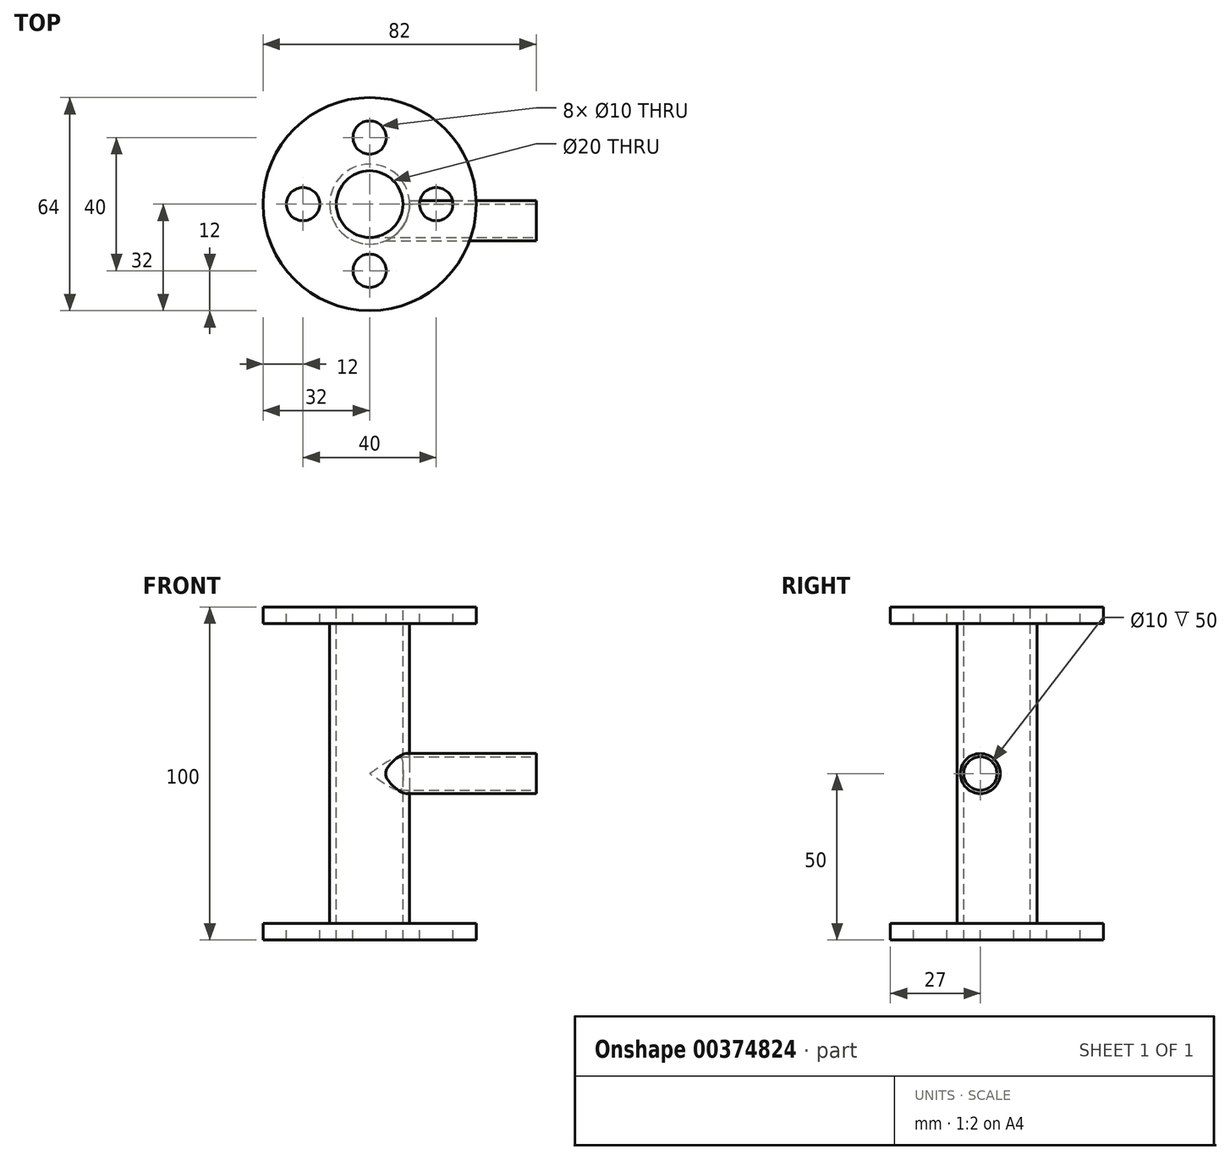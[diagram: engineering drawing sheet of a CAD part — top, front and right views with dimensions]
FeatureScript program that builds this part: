
annotation { "Feature Type Name" : "Feature", "Feature Type Description" : "" }
export const myFeature = defineFeature(function(context is Context, id is Id, definition is map)
    precondition{}
    {
        {
            var Q0;
            Q0=qCreatedBy(makeId("Top.planeOp"),FACE);
            var sketch = newSketch(context, id + "F0", { "sketchPlane" : qUnion([Q0])});
            skCircle(sketch, "E0", {"center": v(0, 0) * mm, "radius": 12 * mm});
            skSolve(sketch);
        }
        {
            var Q0;
            Q0 = qSketchRegion(id + "F0", true);
            extrude(context, id + "F1", {"entities" : qUnion([Q0]), "depth" : 100 * mm, "offsetDistance" : 25 * mm});
        }
        {
            var Q0;
            Q0=makeQuery(id+"F1.opExtrude","CAP_FACE",FACE,{"disambiguationData":[OSD([sQuery(id+"F0.wireOp",EDGE,"E0")])],"isStart":false});
            var sketch = newSketch(context, id + "F2", { "sketchPlane" : qUnion([Q0])});
            skCircle(sketch, "E1", {"center": v(0, 0) * mm, "radius": 10 * mm});
            skSolve(sketch);
        }
        {
            var Q0;
            Q0=makeQuery(id+"F2.imprint","IMPRINT",FACE,{"disambiguationData":[TD([[makeQuery(id+"F2.imprint","IMPRINT",EDGE,{"derivedFrom":sQuery(id+"F2.wireOp",EDGE,"E1")}),1.0]])]});
            var Q1;
            Q1=makeQuery(id+"F1.opExtrude","CAP_FACE",FACE,{"disambiguationData":[OSD([sQuery(id+"F0.wireOp",EDGE,"E0")])],"isStart":true});
            extrude(context, id + "F3", {"entities" : qUnion([Q0]), "operationType" : NewBodyOperationType.REMOVE, "endBound" : BoundingType.UP_TO_SURFACE, "oppositeDirection" : true, "depth" : 25 * mm, "endBoundEntityFace" : qUnion([Q1]), "offsetDistance" : 25 * mm});
        }
        {
            var Q0;
            Q0=makeQuery(id+"F1.opExtrude","CAP_FACE",FACE,{"disambiguationData":[OSD([sQuery(id+"F0.wireOp",EDGE,"E0")])],"isStart":true});
            var sketch = newSketch(context, id + "F4", { "sketchPlane" : qUnion([Q0])});
            skCircle(sketch, "E2", {"center": v(0, 0) * mm, "radius": 32 * mm});
            skSolve(sketch);
        }
        {
            var Q0;
            Q0=makeQuery(id+"F4.imprint","IMPRINT",FACE,{"disambiguationData":[TD([[makeQuery(id+"F4.imprint","IMPRINT",EDGE,{"derivedFrom":sQuery(id+"F4.wireOp",EDGE,"E2")}),1.0]])]});
            extrude(context, id + "F5", {"entities" : qUnion([Q0]), "operationType" : NewBodyOperationType.ADD, "oppositeDirection" : true, "depth" : 5 * mm, "offsetDistance" : 25 * mm});
        }
        {
            var Q0;
            Q0=makeQuery(id+"F1.opExtrude","CAP_FACE",FACE,{"disambiguationData":[OSD([sQuery(id+"F0.wireOp",EDGE,"E0")])],"isStart":false});
            var sketch = newSketch(context, id + "F6", { "sketchPlane" : qUnion([Q0])});
            skCircle(sketch, "E3", {"center": v(0, 0) * mm, "radius": 32 * mm});
            skSolve(sketch);
        }
        {
            var Q0;
            Q0=makeQuery(id+"F6.imprint","IMPRINT",FACE,{"disambiguationData":[TD([[makeQuery(id+"F6.imprint","IMPRINT",EDGE,{"derivedFrom":sQuery(id+"F6.wireOp",EDGE,"E3")}),1.0]])]});
            extrude(context, id + "F7", {"entities" : qUnion([Q0]), "operationType" : NewBodyOperationType.ADD, "oppositeDirection" : true, "depth" : 5 * mm, "offsetDistance" : 25 * mm});
        }
        {
            var Q0;
            {var subQ0=sQuery(id+"F0.wireOp",EDGE,"E0");Q0=makeQuery(id+"F7.boolean.opBoolean","MERGE",FACE,{"derivedFrom":[makeQuery(id+"F1.opExtrude","CAP_FACE",FACE,{"disambiguationData":[OSD([subQ0])],"isStart":false}),makeQuery(id+"F7.opExtrude","CAP_FACE",FACE,{"disambiguationData":[OSD([subQ0,sQuery(id+"F6.wireOp",EDGE,"E3")])],"isStart":true})]});}
            var sketch = newSketch(context, id + "F8", { "sketchPlane" : qUnion([Q0])});
            skCircle(sketch, "E4", {"center": v(0, 20) * mm, "radius": 5 * mm});
            skCircle(sketch, "E5.1.0", {"center": v(-20, 0) * mm, "radius": 5 * mm});
            skCircle(sketch, "E5.2.0", {"center": v(0, -20) * mm, "radius": 5 * mm});
            skCircle(sketch, "E5.3.0", {"center": v(20, 0) * mm, "radius": 5 * mm});
            skPoint(sketch, "E5.center", {"position": v(0, 0) * mm});
            skSolve(sketch);
        }
        {
            var Q0;
            Q0 = qSketchRegion(id + "F8", true);
            var Q1;
            {var subQ0=sQuery(id+"F0.wireOp",EDGE,"E0");Q1=makeQuery(id+"F5.boolean.opBoolean","MERGE",FACE,{"derivedFrom":[makeQuery(id+"F1.opExtrude","CAP_FACE",FACE,{"disambiguationData":[OSD([subQ0])],"isStart":true}),makeQuery(id+"F5.opExtrude","CAP_FACE",FACE,{"disambiguationData":[OSD([subQ0,sQuery(id+"F4.wireOp",EDGE,"E2")])],"isStart":true})]});}
            extrude(context, id + "F9", {"entities" : qUnion([Q0]), "operationType" : NewBodyOperationType.REMOVE, "endBound" : BoundingType.UP_TO_SURFACE, "oppositeDirection" : true, "depth" : 25 * mm, "endBoundEntityFace" : qUnion([Q1]), "offsetDistance" : 25 * mm});
        }
        {
            var Q0;
            Q0=qCreatedBy(makeId("Right.planeOp"),FACE);
            var sketch = newSketch(context, id + "F10", { "sketchPlane" : qUnion([Q0])});
            skLineSegment(sketch, "E6", {"start": v(0, 0) * mm, "end": v(0, 50) * mm});
            skLineSegment(sketch, "E7", {"start": v(0, 50) * mm, "end": v(-5, 50) * mm});
            skCircle(sketch, "E8", {"center": v(-5, 50) * mm, "radius": 6 * mm});
            skSolve(sketch);
        }
        {
            var Q0;
            Q0=qCreatedBy(makeId("Front.planeOp"),FACE);
            cPlane(context, id + "F11", {"entities" : qUnion([Q0]), "cplaneType" : CPlaneType.OFFSET, "offset" : 5 * mm, "width" : 150 * mm, "height" : 150 * mm});
        }
        {
            var Q0;
            Q0=qCreatedBy(id+"F11.planeOp",FACE);
            var sketch = newSketch(context, id + "F12", { "sketchPlane" : qUnion([Q0])});
            skLineSegment(sketch, "E9", {"start": v(0, 50) * mm, "end": v(50, 50) * mm});
            skSolve(sketch);
        }
        {
            var Q0;
            Q0=makeQuery(id+"F10.imprint","IMPRINT",FACE,{"disambiguationData":[TD([[makeQuery(id+"F10.imprint","IMPRINT",EDGE,{"derivedFrom":sQuery(id+"F10.wireOp",EDGE,"E8")}),1.0]])]});
            var Q1;
            Q1=sQuery(id+"F12.wireOp",EDGE,"E9");
            sweep(context, id + "F13", {"operationType" : NewBodyOperationType.ADD, "profiles" : qUnion([Q0]), "path" : qUnion([Q1])});
        }
        {
            var Q0;
            Q0=makeQuery(id+"F13.opSweep","CAP_FACE",FACE,{"disambiguationData":[OSD([sQuery(id+"F10.wireOp",EDGE,"E8"),sQuery(id+"F12.wireOp",VERTEX,"E9.end")])],"isStart":false});
            var sketch = newSketch(context, id + "F14", { "sketchPlane" : qUnion([Q0])});
            skCircle(sketch, "E10", {"center": v(-5, 50) * mm, "radius": 5 * mm});
            skSolve(sketch);
        }
        {
            var Q0;
            Q0 = qSketchRegion(id + "F14", true);
            var Q1;
            Q1=makeQuery(id+"F13.opSweep","CAP_FACE",FACE,{"disambiguationData":[OSD([sQuery(id+"F10.wireOp",EDGE,"E8"),sQuery(id+"F12.wireOp",VERTEX,"E9.start")])],"isStart":true});
            extrude(context, id + "F15", {"entities" : qUnion([Q0]), "operationType" : NewBodyOperationType.REMOVE, "endBound" : BoundingType.UP_TO_SURFACE, "oppositeDirection" : true, "depth" : 25 * mm, "endBoundEntityFace" : qUnion([Q1]), "offsetDistance" : 25 * mm});
        }
        {
            var Q0;
            {var subQ0=sQuery(id+"F0.wireOp",EDGE,"E0");Q0=makeQuery(id+"F7.boolean.opBoolean","MERGE",FACE,{"derivedFrom":[makeQuery(id+"F1.opExtrude","CAP_FACE",FACE,{"disambiguationData":[OSD([subQ0])],"isStart":false}),makeQuery(id+"F7.opExtrude","CAP_FACE",FACE,{"disambiguationData":[OSD([subQ0,sQuery(id+"F6.wireOp",EDGE,"E3")])],"isStart":true})]});}
            var sketch = newSketch(context, id + "F16", { "sketchPlane" : qUnion([Q0])});
            skCircle(sketch, "E11", {"center": v(0, 0) * mm, "radius": 10 * mm});
            skSolve(sketch);
        }
        {
            var Q0;
            Q0 = qSketchRegion(id + "F16", true);
            extrude(context, id + "F17", {"entities" : qUnion([Q0]), "operationType" : NewBodyOperationType.REMOVE, "oppositeDirection" : true, "depth" : 70 * mm, "offsetDistance" : 25 * mm});
        }
    });
